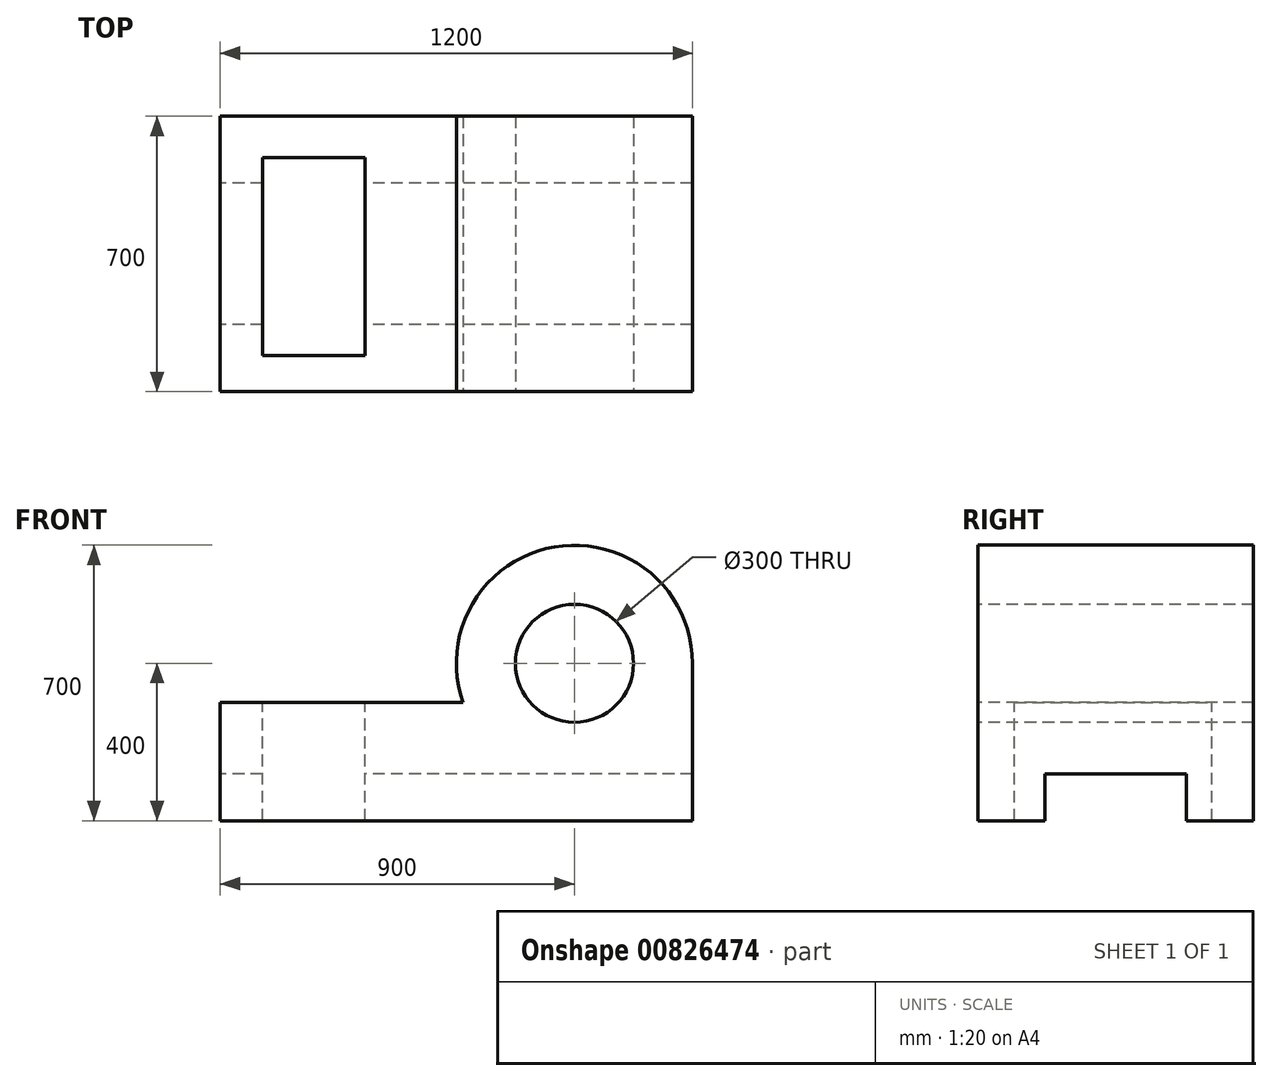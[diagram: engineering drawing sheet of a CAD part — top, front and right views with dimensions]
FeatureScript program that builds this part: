
annotation { "Feature Type Name" : "Feature", "Feature Type Description" : "" }
export const myFeature = defineFeature(function(context is Context, id is Id, definition is map)
    precondition{}
    {
        {
            var Q0;
            Q0=qCreatedBy(makeId("Front.planeOp"),FACE);
            var sketch = newSketch(context, id + "F0", { "sketchPlane" : qUnion([Q0])});
            skLineSegment(sketch, "E0.bottom", {"start": v(-600, -350) * mm, "end": v(600, -350) * mm});
            skLineSegment(sketch, "E0.top", {"start": v(-600, 350) * mm, "end": v(600, 350) * mm});
            skLineSegment(sketch, "E0.left", {"start": v(-600, -350) * mm, "end": v(-600, 350) * mm});
            skLineSegment(sketch, "E0.right", {"start": v(600, -350) * mm, "end": v(600, 350) * mm});
            skPoint(sketch, "E0.middle", {"position": v(0, 0) * mm});
            skSolve(sketch);
        }
        {
            var Q0;
            Q0=makeQuery(id+"F0.imprint","IMPRINT",FACE,{"disambiguationData":[TD([[makeQuery(id+"F0.imprint","IMPRINT",EDGE,{"derivedFrom":sQuery(id+"F0.wireOp",EDGE,"E0.bottom")}),1.0]])]});
            extrude(context, id + "F1", {"entities" : qUnion([Q0]), "depth" : 700 * mm, "offsetDistance" : 25 * mm});
        }
        {
            var Q0;
            Q0=makeQuery(id+"F1.opExtrude","CAP_FACE",FACE,{"disambiguationData":[OSD([sQuery(id+"F0.wireOp",EDGE,"E0.bottom"),sQuery(id+"F0.wireOp",EDGE,"E0.top"),sQuery(id+"F0.wireOp",EDGE,"E0.left"),sQuery(id+"F0.wireOp",EDGE,"E0.right")])],"isStart":false});
            var sketch = newSketch(context, id + "F2", { "sketchPlane" : qUnion([Q0])});
            skCircle(sketch, "E1", {"center": v(300, 50) * mm, "radius": 300 * mm});
            skPoint(sketch, "E2.start.orphan", {"position": v(-600, 0) * mm});
            skLineSegment(sketch, "E3", {"start": v(-600, -350) * mm, "end": v(-600, -50) * mm});
            skLineSegment(sketch, "E4", {"start": v(-600, -50) * mm, "end": v(17.16, -50) * mm});
            skSolve(sketch);
        }
        {
            var Q0;
            {var subQ0=sQuery(id+"F2.wireOp",EDGE,"E4");Q0=makeQuery(id+"F2.imprint","IMPRINT",FACE,{"disambiguationData":[TD([[makeQuery(id+"F2.imprint","IMPRINT",EDGE,{"derivedFrom":subQ0}),1.0]])]});}
            var Q1;
            {var subQ0=sQuery(id+"F2.wireOp",EDGE,"E1");var subQ1=makeQuery(id+"F1.opExtrude","CAP_EDGE",EDGE,{"disambiguationData":[OSD([sQuery(id+"F0.wireOp",EDGE,"E0.top")])],"isStart":false});var subQ2=makeQuery(id+"F2.imprint","INTERSECT",VERTEX,{"derivedFrom":[subQ1,subQ0]});Q1=makeQuery(id+"F2.imprint","IMPRINT",FACE,{"disambiguationData":[TD([[makeQuery(id+"F2.imprint","IMPRINT",EDGE,{"disambiguationData":[TD([[subQ2,1.0]])],"derivedFrom":subQ0}),-1.0]])]});}
            extrude(context, id + "F3", {"entities" : qUnion([Q0, Q1]), "operationType" : NewBodyOperationType.REMOVE, "endBound" : BoundingType.THROUGH_ALL, "oppositeDirection" : true, "depth" : 25 * mm, "offsetDistance" : 25 * mm});
        }
        {
            var Q0;
            Q0=makeQuery(id+"F1.opExtrude","CAP_FACE",FACE,{"disambiguationData":[OSD([sQuery(id+"F0.wireOp",EDGE,"E0.bottom"),sQuery(id+"F0.wireOp",EDGE,"E0.top"),sQuery(id+"F0.wireOp",EDGE,"E0.left"),sQuery(id+"F0.wireOp",EDGE,"E0.right")])],"isStart":false});
            var sketch = newSketch(context, id + "F4", { "sketchPlane" : qUnion([Q0])});
            skCircle(sketch, "E5", {"center": v(300, 50) * mm, "radius": 150 * mm});
            skSolve(sketch);
        }
        {
            var Q0;
            Q0 = qSketchRegion(id + "F4", true);
            extrude(context, id + "F5", {"entities" : qUnion([Q0]), "operationType" : NewBodyOperationType.REMOVE, "endBound" : BoundingType.THROUGH_ALL, "oppositeDirection" : true, "depth" : 25 * mm, "offsetDistance" : 25 * mm});
        }
        {
            var Q0;
            Q0=makeQuery(id+"F3.boolean.opBoolean","COPY",FACE,{"derivedFrom":makeQuery(id+"F3.opExtrude","SWEPT_FACE",FACE,{"disambiguationData":[OSD([sQuery(id+"F2.wireOp",EDGE,"E4")])]})});
            var sketch = newSketch(context, id + "F6", { "sketchPlane" : qUnion([Q0])});
            skLineSegment(sketch, "E6.bottom", {"start": v(-232.42, -504.54) * mm, "end": v(-492.42, -504.54) * mm});
            skLineSegment(sketch, "E6.top", {"start": v(-232.42, -105.7) * mm, "end": v(-492.42, -105.7) * mm});
            skLineSegment(sketch, "E6.left", {"start": v(-232.42, -504.54) * mm, "end": v(-232.42, -105.7) * mm});
            skLineSegment(sketch, "E6.right", {"start": v(-492.42, -504.54) * mm, "end": v(-492.42, -105.7) * mm});
            skPoint(sketch, "E6.middle", {"position": v(-362.42, -305.12) * mm});
            skSolve(sketch);
        }
        {
            var Q0;
            Q0=makeQuery(id+"F6.imprint","IMPRINT",FACE,{"disambiguationData":[TD([[makeQuery(id+"F6.imprint","IMPRINT",EDGE,{"derivedFrom":sQuery(id+"F6.wireOp",EDGE,"E6.bottom")}),-1.0]])]});
            extrude(context, id + "F7", {"entities" : qUnion([Q0]), "operationType" : NewBodyOperationType.REMOVE, "endBound" : BoundingType.THROUGH_ALL, "oppositeDirection" : true, "depth" : 25 * mm, "offsetDistance" : 25 * mm});
        }
        {
            var Q0;
            Q0=makeQuery(id+"F3.boolean.opBoolean","COPY",FACE,{"derivedFrom":makeQuery(id+"F3.opExtrude","SWEPT_FACE",FACE,{"disambiguationData":[OSD([sQuery(id+"F2.wireOp",EDGE,"E4")])]})});
            var sketch = newSketch(context, id + "F8", { "sketchPlane" : qUnion([Q0])});
            skLineSegment(sketch, "E7", {"start": v(-492.42, -504.54) * mm, "end": v(-492.42, -607.52) * mm});
            skLineSegment(sketch, "E8", {"start": v(-492.42, -607.52) * mm, "end": v(-232.42, -607.52) * mm});
            skLineSegment(sketch, "E9", {"start": v(-232.42, -607.52) * mm, "end": v(-232.42, -504.54) * mm});
            skLineSegment(sketch, "E10", {"start": v(-232.42, -504.54) * mm, "end": v(-492.42, -504.54) * mm});
            skSolve(sketch);
        }
        {
            var Q0;
            Q0 = qSketchRegion(id + "F8", true);
            extrude(context, id + "F9", {"entities" : qUnion([Q0]), "operationType" : NewBodyOperationType.REMOVE, "endBound" : BoundingType.THROUGH_ALL, "oppositeDirection" : true, "depth" : 25 * mm, "offsetDistance" : 25 * mm});
        }
        {
            var Q0;
            Q0=makeQuery(id+"F1.opExtrude","SWEPT_FACE",FACE,{"disambiguationData":[OSD([sQuery(id+"F0.wireOp",EDGE,"E0.left")])]});
            var sketch = newSketch(context, id + "F10", { "sketchPlane" : qUnion([Q0])});
            skLineSegment(sketch, "E11.bottom", {"start": v(170.03, -231.48) * mm, "end": v(529.97, -231.48) * mm});
            skLineSegment(sketch, "E11.top", {"start": v(170.03, -468.52) * mm, "end": v(529.97, -468.52) * mm});
            skLineSegment(sketch, "E11.left", {"start": v(170.03, -231.48) * mm, "end": v(170.03, -468.52) * mm});
            skLineSegment(sketch, "E11.right", {"start": v(529.97, -231.48) * mm, "end": v(529.97, -468.52) * mm});
            skPoint(sketch, "E11.middle", {"position": v(350, -350) * mm});
            skSolve(sketch);
        }
        {
            var Q0;
            Q0 = qSketchRegion(id + "F10", true);
            extrude(context, id + "F11", {"entities" : qUnion([Q0]), "operationType" : NewBodyOperationType.REMOVE, "endBound" : BoundingType.THROUGH_ALL, "oppositeDirection" : true, "depth" : 25 * mm, "offsetDistance" : 25 * mm});
        }
    });
